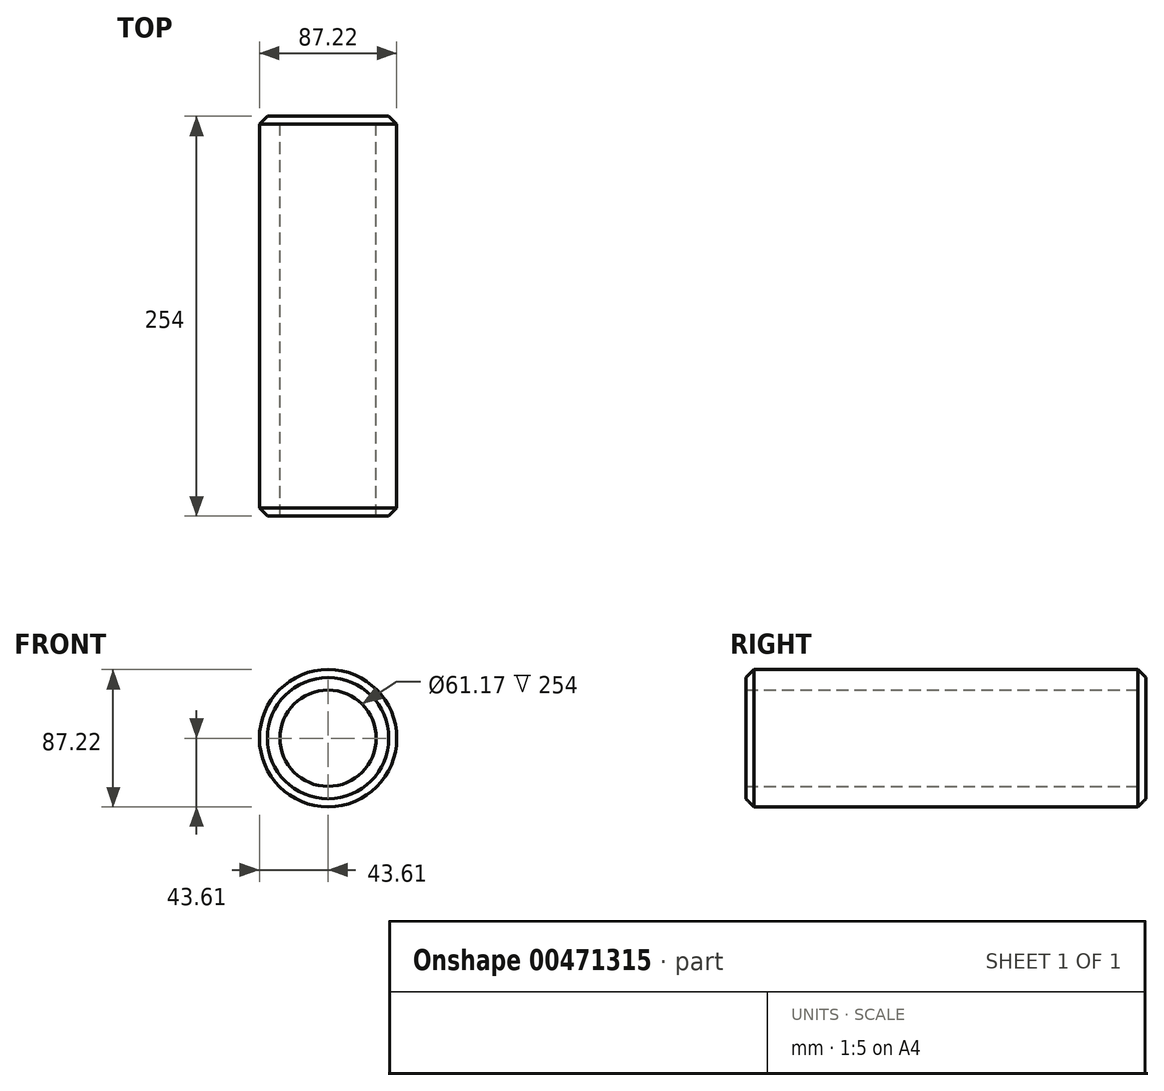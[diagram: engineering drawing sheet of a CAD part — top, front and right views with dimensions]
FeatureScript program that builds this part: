
annotation { "Feature Type Name" : "Feature", "Feature Type Description" : "" }
export const myFeature = defineFeature(function(context is Context, id is Id, definition is map)
    precondition{}
    {
        {
            var Q0;
            Q0=qCreatedBy(makeId("Front.planeOp"),FACE);
            var sketch = newSketch(context, id + "F0", { "sketchPlane" : qUnion([Q0])});
            skCircle(sketch, "E0", {"center": v(0, 0) * mm, "radius": 43.6 * mm});
            skCircle(sketch, "E1", {"center": v(0, 0) * mm, "radius": 30.59 * mm});
            skSolve(sketch);
        }
        {
            var Q0;
            Q0=makeQuery(id+"F0.imprint","IMPRINT",FACE,{"disambiguationData":[TD([[makeQuery(id+"F0.imprint","IMPRINT",EDGE,{"derivedFrom":sQuery(id+"F0.wireOp",EDGE,"E0")}),1.0]])]});
            extrude(context, id + "F1", {"entities" : qUnion([Q0]), "depth" : 254 * mm});
        }
        {
            var Q0;
            Q0=qCreatedBy(makeId("Top.planeOp"),FACE);
            var sketch = newSketch(context, id + "F2", { "sketchPlane" : qUnion([Q0])});
            skCircle(sketch, "E2", {"center": v(0, -72.36) * mm, "radius": 23.86 * mm});
            skCircle(sketch, "E3", {"center": v(0, -72.36) * mm, "radius": 13.89 * mm});
            skSolve(sketch);
        }
        {
            var Q0;
            Q0=sQuery(id+"F2.wireOp",EDGE,"E2");
            var Q1;
            Q1=sQuery(id+"F2.wireOp",EDGE,"E3");
            extrude(context, id + "F3", {"bodyType" : ToolBodyType.SURFACE, "surfaceEntities" : qUnion([Q0, Q1]), "depth" : 76.2 * mm});
        }
        {
            var Q0;
            Q0=makeQuery(id+"F1.opExtrude","SWEPT_FACE",FACE,{"disambiguationData":[OSD([sQuery(id+"F0.wireOp",EDGE,"E0")])]});
            chamfer(context, id + "F4", {"entities" : qUnion([Q0]), "width" : 5.08 * mm, "tangentPropagation" : true});
        }
    });
